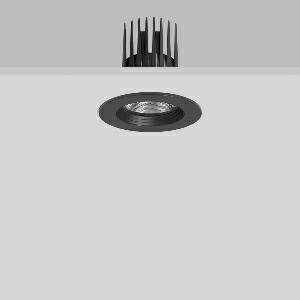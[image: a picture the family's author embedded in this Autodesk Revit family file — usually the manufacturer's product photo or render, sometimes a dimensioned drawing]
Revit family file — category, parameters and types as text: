
# Revit family: heledon_mini_e_901740_003_2_76_1ee8
name_source: partatom
category: Lighting Fixtures
units: mm (PartAtom-declared; Revit-internal decimal feet)

## family parameters
Cut with Voids When Loaded = No
Host = Face
Light Source = No
Part Type = Normal
Room Calculation Point = No
Round Connector Dimension = Use Diameter
Shared = No

## types (1)
- HELEDON mini E (1 x LED Modul 927, 2400 lm, 2700)
    Apparent Load = 20 VA
    Approval mark = CE
    CIE Flux Codes = 100 100 100 100 100
    Color Rendering = 92
    Color Temperature = 2700
    Default Elevation = 1800 mm
    Description = Series: HELEDON mini
Round recessed downlight. Housing: die-cast aluminium, powder-coated. Black plastic ring and recessed LED to prevent glare from the side. Optical assembly with reflector made of MIRO-Silver with 98% total light reflection for outstanding efficiency - can be changed without tools. Best colour rendering index Ra>90. Suitable for Recessed ceiling mounting. Installation without tools thanks to spring fastening system. Including separate LED converter with connecting cable 600 mm.High quality converter without flickering and stroboscopic effect. Through-wiring box (5 pole) available as accessory. The following accessories can be mounted without use of tools: interchangeable lenses, decorative glasses, honeycomb louvre, clear and frosted diffusers, white interchangeable plastic ring. 
Colour: deep black, matt (RAL 9005)
Diameter: 124 mm
Height: 3 mm
Cut-out diameter: 114 mm
Recess height: 170 mm
Luminaire: recess height: 120 mm
Lamp: LED
Socket: without socket
Colour temperature: 2700K
Colour rendering index (CRI): 92
System power: 20 W
Rated luminous flux: 2400 lm
Luminous efficiency: 120 lm/W
Control gear: Converter, dimmable, DALI
Protection class: II
Type of protection: IP 20
    Height = 0 mm  [stored 0 ft]
    Lamp = 1 x LED Modul 927
    Lamp Light Flux = 2400 lm
    Lamp count = 1
    Length = 124 mm  [stored 0.406824 ft]
    Lifetime = 50000 h
    Luminous efficacy = 120 lm/W
    Manufacturer = RZB
    ModVariant = No
    Model = 901740.003.2.76
    Mounting Place = Ceiling
    Mounting Type = Recessed
    Number of Poles = 1
    OnlyDefault = Yes
    Power Factor = 1
    Product Name = HELEDON mini E
    Product group = Recessed downlights
    ProductGroupID = 402
    Protection Class = Protection class II
    Protection Degree = IP 20
    RLX_Detail_Level = 1
    RLX_Emergency_Light_Flux = 0 lm
    RLX_Emergency_Type = 0
    RLX_Emergency_Type_DB = No
    RlxData = <blob elided: 125877 chars, md5=9c1aae30>
    Socket = socket
    Standby Power = 0 W
    System Light Flux = 2400 lm
    System Power = 20 W
    Type Comments = Product without accessories
    Type Image = 901657.003.jpg
    URL = http://relux.com
    VarID = ---
    Voltage = 230 V
    Voltage Range = 220-240 V
    Weight = 0.00 kg
    Width = 0 mm  [stored 0 ft]

note: [stored X ft] marks values corroborated as IEEE doubles in the binary element streams (Revit-internal decimal feet)

## geometry (parser evidence)
native form markers: Blend x4, Sweep x10
no freeform markers — native parametric forms only
